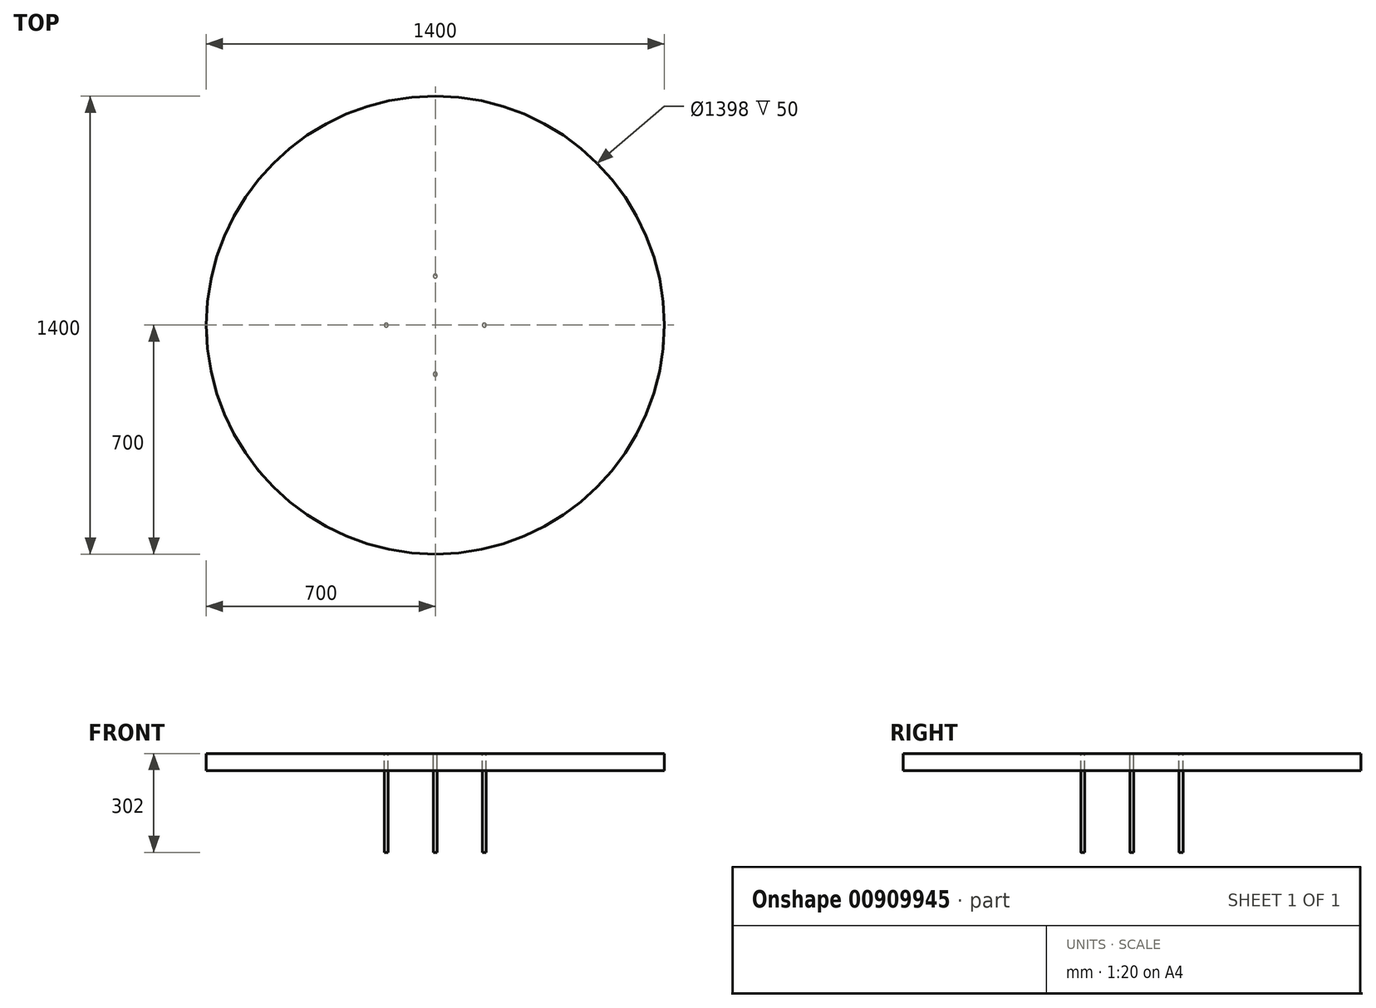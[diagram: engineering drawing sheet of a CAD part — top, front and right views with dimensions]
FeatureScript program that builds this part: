
annotation { "Feature Type Name" : "Feature", "Feature Type Description" : "" }
export const myFeature = defineFeature(function(context is Context, id is Id, definition is map)
    precondition{}
    {
        {
            var Q0;
            Q0=qCreatedBy(makeId("Top.planeOp"),FACE);
            var sketch = newSketch(context, id + "F0", { "sketchPlane" : qUnion([Q0])});
            skCircle(sketch, "E0", {"center": v(0, 0) * mm, "radius": 700 * mm});
            skSolve(sketch);
        }
        {
            var Q0;
            Q0 = qSketchRegion(id + "F0", true);
            extrude(context, id + "F1", {"entities" : qUnion([Q0]), "depth" : 2 * mm, "offsetDistance" : 25 * mm});
        }
        {
            var Q0;
            Q0=makeQuery(id+"F1.opExtrude","CAP_FACE",FACE,{"disambiguationData":[OSD([sQuery(id+"F0.wireOp",EDGE,"E0")])],"isStart":true});
            var sketch = newSketch(context, id + "F2", { "sketchPlane" : qUnion([Q0])});
            skCircle(sketch, "E1", {"center": v(0, 0) * mm, "radius": 700 * mm});
            skCircle(sketch, "E2", {"center": v(0, 0) * mm, "radius": 699 * mm});
            skSolve(sketch);
        }
        {
            var Q0;
            Q0 = qSketchRegion(id + "F2", true);
            extrude(context, id + "F3", {"entities" : qUnion([Q0]), "operationType" : NewBodyOperationType.ADD, "depth" : 50 * mm, "offsetDistance" : 25 * mm});
        }
        {
            var Q0;
            Q0=makeQuery(id+"F1.opExtrude","CAP_FACE",FACE,{"disambiguationData":[OSD([sQuery(id+"F0.wireOp",EDGE,"E0")])],"isStart":true});
            var sketch = newSketch(context, id + "F4", { "sketchPlane" : qUnion([Q0])});
            skCircle(sketch, "E3", {"center": v(0, 0) * mm, "radius": 350 * mm});
            skCircle(sketch, "E4", {"center": v(0, 150) * mm, "radius": 6 * mm});
            skCircle(sketch, "E5", {"center": v(0, -150) * mm, "radius": 6 * mm});
            skCircle(sketch, "E6", {"center": v(150, 0) * mm, "radius": 6 * mm});
            skCircle(sketch, "E7", {"center": v(-150, 0) * mm, "radius": 6 * mm});
            skSolve(sketch);
        }
        {
            var Q0;
            Q0=makeQuery(id+"F4.imprint","IMPRINT",FACE,{"disambiguationData":[TD([[makeQuery(id+"F4.imprint","IMPRINT",EDGE,{"derivedFrom":sQuery(id+"F4.wireOp",EDGE,"E7")}),1.0]])]});
            var Q1;
            Q1=makeQuery(id+"F4.imprint","IMPRINT",FACE,{"disambiguationData":[TD([[makeQuery(id+"F4.imprint","IMPRINT",EDGE,{"derivedFrom":sQuery(id+"F4.wireOp",EDGE,"E4")}),1.0]])]});
            var Q2;
            Q2=makeQuery(id+"F4.imprint","IMPRINT",FACE,{"disambiguationData":[TD([[makeQuery(id+"F4.imprint","IMPRINT",EDGE,{"derivedFrom":sQuery(id+"F4.wireOp",EDGE,"E6")}),1.0]])]});
            var Q3;
            Q3=makeQuery(id+"F4.imprint","IMPRINT",FACE,{"disambiguationData":[TD([[makeQuery(id+"F4.imprint","IMPRINT",EDGE,{"derivedFrom":sQuery(id+"F4.wireOp",EDGE,"E5")}),1.0]])]});
            extrude(context, id + "F5", {"entities" : qUnion([Q0, Q1, Q2, Q3]), "operationType" : NewBodyOperationType.ADD, "depth" : 300 * mm, "offsetDistance" : 25 * mm});
        }
    });
